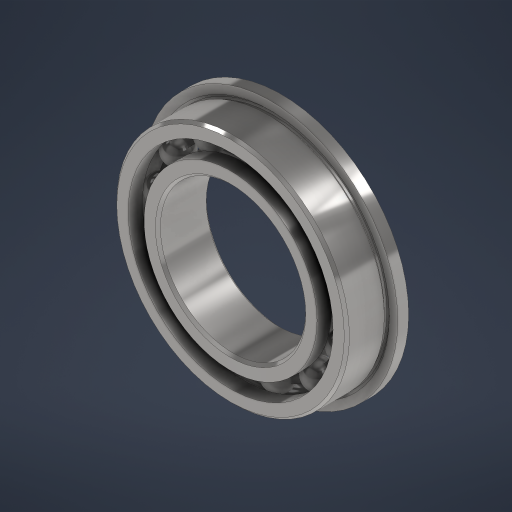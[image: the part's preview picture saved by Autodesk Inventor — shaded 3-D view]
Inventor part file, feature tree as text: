
AUTODESK INVENTOR PART (.ipt)
format: ipt  version: 2024 (Build 280153000, 153)  size: 775,680 bytes
history: native  units: in
note: dims shown in document units (in); Inventor stores cm internally (conversion verified against a paired STEP export)
features: other x12, revolve x4
ambient origin geometry x8: Origin, YZ Plane, XZ Plane, XY Plane, X Axis, Y Axis, Z Axis, Center Point
bodies: Solid1 (feature_tree), Solid2 (feature_tree), Solid3 (feature_tree), Solid4 (feature_tree), Solid5 (feature_tree), Solid6 (feature_tree), Solid7 (feature_tree), Solid8 (feature_tree), Solid9 (feature_tree), Solid10 (feature_tree), Solid11 (feature_tree), Solid12 (feature_tree), Solid13 (feature_tree), Solid14 (feature_tree), Solid15 (feature_tree), Solid16 (feature_tree)
feature tree (16):
  revolve  "Revolve1"  [1 undecoded]
  revolve  "Revolve3"  [1 undecoded]
  revolve  "Revolve4"  [1 undecoded]
  other  "CirPattern1[1]"
  other  "CirPattern1[2]"
  other  "CirPattern1[3]"
  other  "CirPattern1[4]"
  other  "CirPattern1[5]"
  other  "CirPattern1[6]"
  other  "CirPattern1[7]"
  other  "CirPattern1[8]"
  other  "CirPattern1[9]"
  other  "CirPattern1[10]"
  other  "CirPattern1[11]"
  other  "CirPattern1[12]"
  revolve  "Revolve6"  [1 undecoded]
note: 4 required parameter values undecoded (feature->parameter linkage not recoverable at this tier; creation-order binding heuristic only, values carry confidence <= 0.55)
